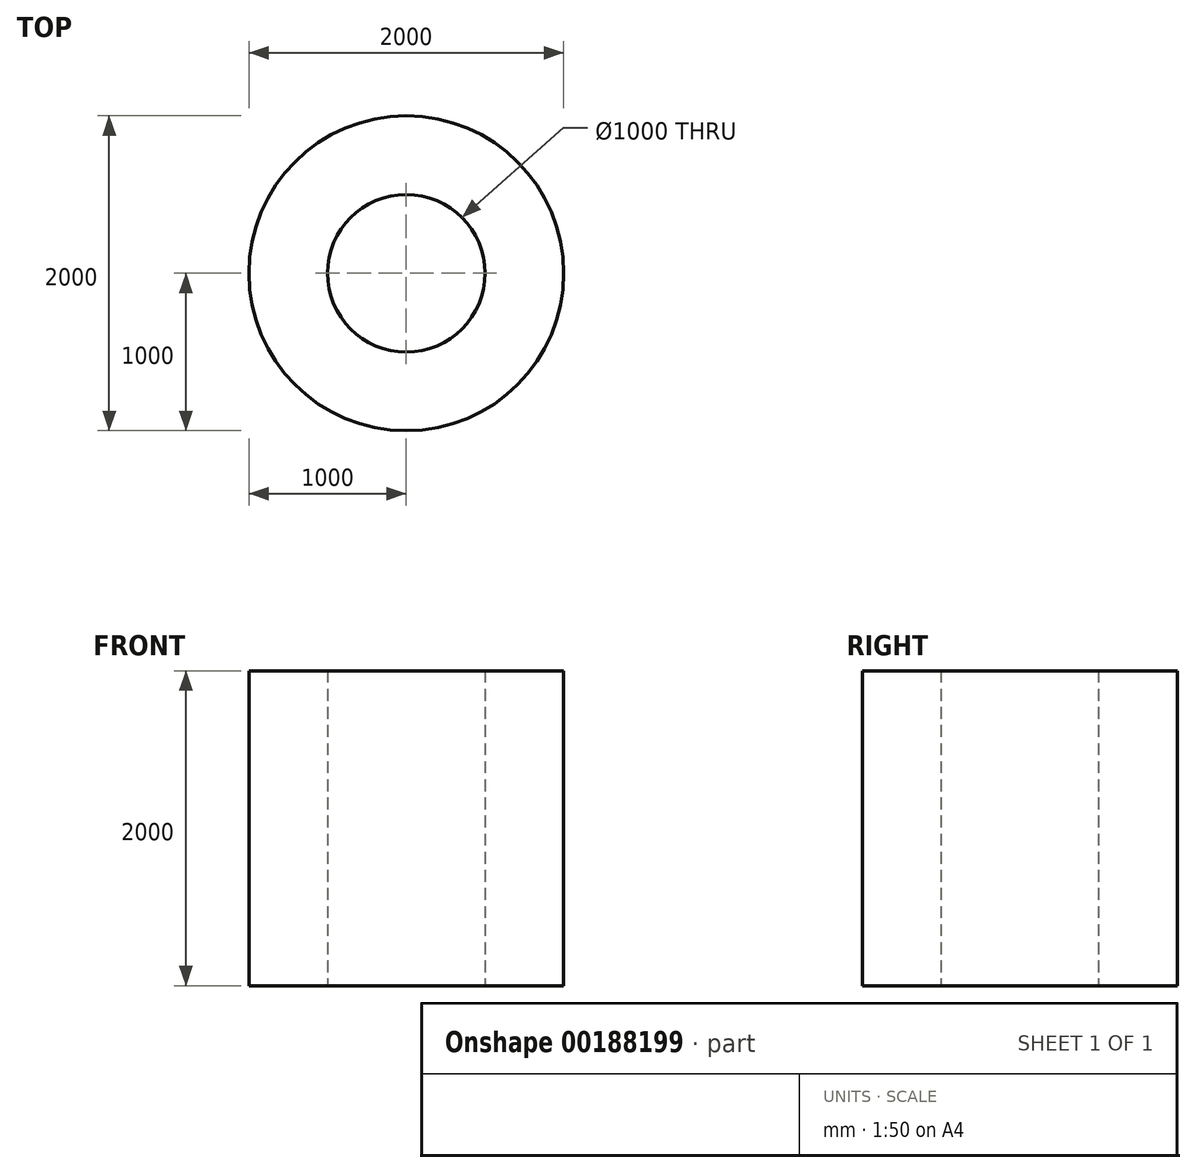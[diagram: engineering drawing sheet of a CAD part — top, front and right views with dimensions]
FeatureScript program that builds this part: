
annotation { "Feature Type Name" : "Feature", "Feature Type Description" : "" }
export const myFeature = defineFeature(function(context is Context, id is Id, definition is map)
    precondition{}
    {
        {
            var Q0;
            Q0=qCreatedBy(makeId("Top.planeOp"),FACE);
            var sketch = newSketch(context, id + "F0", { "sketchPlane" : qUnion([Q0])});
            skCircle(sketch, "E0", {"center": v(0, 0) * mm, "radius": 1000 * mm});
            skCircle(sketch, "E1", {"center": v(0, 0) * mm, "radius": 500 * mm});
            skSolve(sketch);
        }
        {
            var Q0;
            Q0=makeQuery(id+"F0.imprint","IMPRINT",FACE,{"disambiguationData":[TD([[makeQuery(id+"F0.imprint","IMPRINT",EDGE,{"derivedFrom":sQuery(id+"F0.wireOp",EDGE,"E0")}),1.0]])]});
            extrude(context, id + "F1", {"entities" : qUnion([Q0]), "depth" : 2000 * mm});
        }
    });
